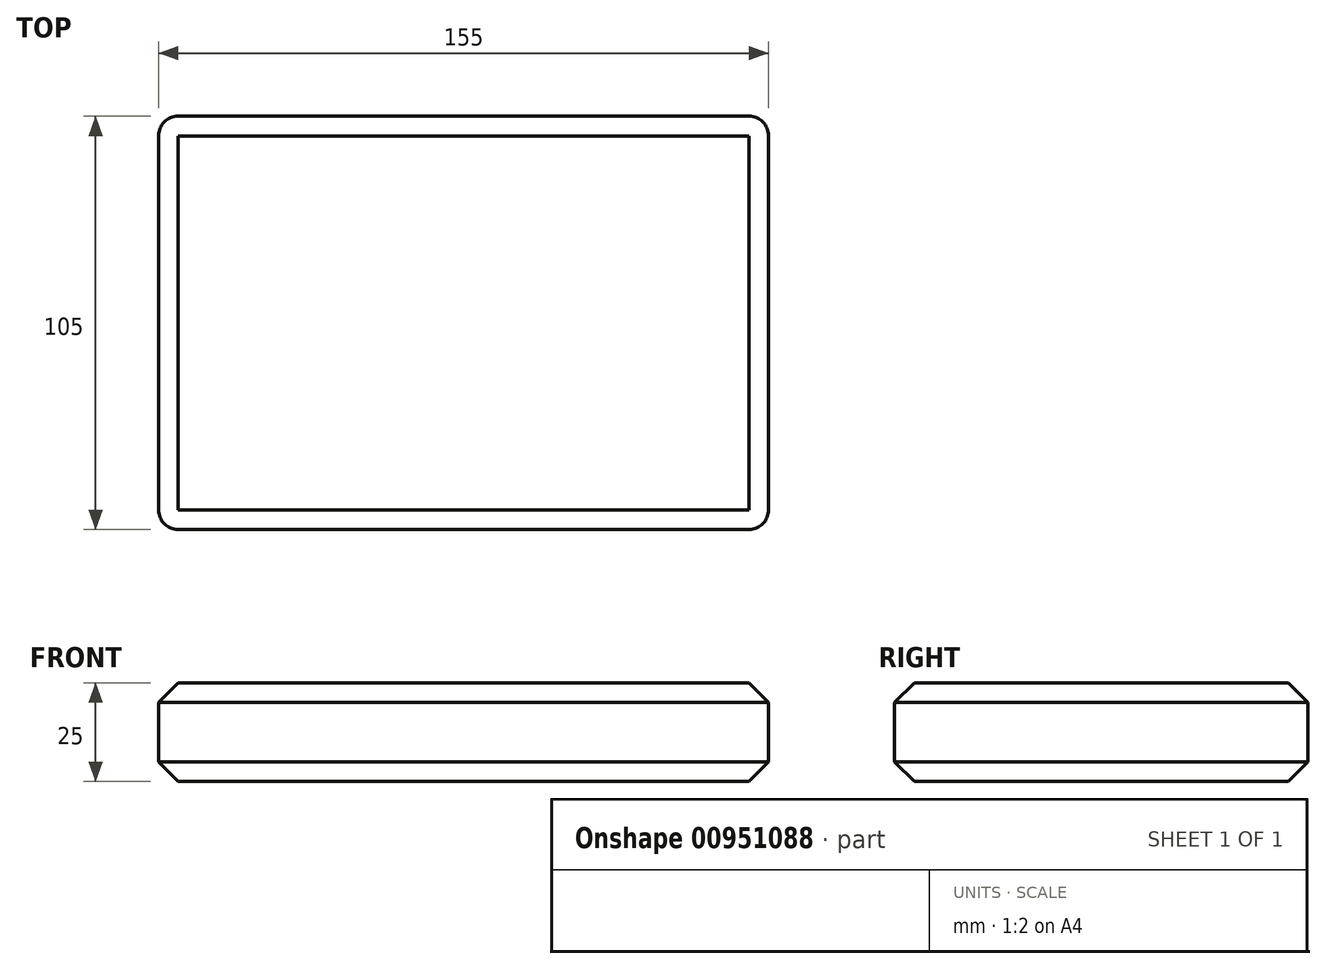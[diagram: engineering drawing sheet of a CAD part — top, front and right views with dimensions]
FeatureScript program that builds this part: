
annotation { "Feature Type Name" : "Feature", "Feature Type Description" : "" }
export const myFeature = defineFeature(function(context is Context, id is Id, definition is map)
    precondition{}
    {
        {
            var Q0;
            Q0=qCreatedBy(makeId("Top.planeOp"),FACE);
            var sketch = newSketch(context, id + "F0", { "sketchPlane" : qUnion([Q0])});
            skLineSegment(sketch, "E0.bottom", {"start": v(-77.5, 52.5) * mm, "end": v(77.5, 52.5) * mm});
            skLineSegment(sketch, "E0.top", {"start": v(-77.5, -52.5) * mm, "end": v(77.5, -52.5) * mm});
            skLineSegment(sketch, "E0.left", {"start": v(-77.5, 52.5) * mm, "end": v(-77.5, -52.5) * mm});
            skLineSegment(sketch, "E0.right", {"start": v(77.5, 52.5) * mm, "end": v(77.5, -52.5) * mm});
            skSolve(sketch);
        }
        {
            var Q0;
            Q0=makeQuery(id+"F0.imprint","IMPRINT",FACE,{"disambiguationData":[TD([[makeQuery(id+"F0.imprint","IMPRINT",EDGE,{"derivedFrom":sQuery(id+"F0.wireOp",EDGE,"E0.bottom")}),-1.0]])]});
            extrude(context, id + "F1", {"entities" : qUnion([Q0]), "depth" : 25 * mm, "offsetDistance" : 25 * mm});
        }
        {
            var Q0;
            Q0=makeQuery(id+"F1.opExtrude","SWEPT_EDGE",EDGE,{"disambiguationData":[OSD([sQuery(id+"F0.wireOp",EDGE,"E0.top"),sQuery(id+"F0.wireOp",EDGE,"E0.left")])]});
            var Q1;
            Q1=makeQuery(id+"F1.opExtrude","SWEPT_EDGE",EDGE,{"disambiguationData":[OSD([sQuery(id+"F0.wireOp",EDGE,"E0.bottom"),sQuery(id+"F0.wireOp",EDGE,"E0.left")])]});
            var Q2;
            Q2=makeQuery(id+"F1.opExtrude","SWEPT_EDGE",EDGE,{"disambiguationData":[OSD([sQuery(id+"F0.wireOp",EDGE,"E0.top"),sQuery(id+"F0.wireOp",EDGE,"E0.right")])]});
            var Q3;
            Q3=makeQuery(id+"F1.opExtrude","SWEPT_EDGE",EDGE,{"disambiguationData":[OSD([sQuery(id+"F0.wireOp",EDGE,"E0.bottom"),sQuery(id+"F0.wireOp",EDGE,"E0.right")])]});
            fillet(context, id + "F2", {"entities" : qUnion([Q0, Q1, Q2, Q3]), "radius" : 5 * mm, "tangentPropagation" : true, "allowEdgeOverflow" : false});
        }
        {
            var Q0;
            Q0=makeQuery(id+"F1.opExtrude","CAP_EDGE",EDGE,{"disambiguationData":[OSD([sQuery(id+"F0.wireOp",EDGE,"E0.bottom")])],"isStart":false});
            var Q1;
            Q1=makeQuery(id+"F1.opExtrude","CAP_EDGE",EDGE,{"disambiguationData":[OSD([sQuery(id+"F0.wireOp",EDGE,"E0.top")])],"isStart":true});
            chamfer(context, id + "F3", {"entities" : qUnion([Q0, Q1]), "width" : 5 * mm, "tangentPropagation" : true});
        }
    });
